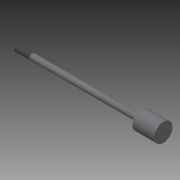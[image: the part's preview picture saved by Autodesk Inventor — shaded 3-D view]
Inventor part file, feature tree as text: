
AUTODESK INVENTOR PART (.ipt)
format: ipt  version: 2014 (Build 180170000, 170)  size: 125,440 bytes
history: native  units: in
note: dims shown in document units (in); Inventor stores cm internally (conversion verified against a paired STEP export)
features: other x49, revolve x3, sketch x3, thread x1
ambient origin geometry x8: Origin, YZ Plane, XZ Plane, XY Plane, X Axis, Y Axis, Z Axis, Center Point
bodies: Solid1 (feature_tree)
feature tree (56):
  revolve  "Revolution1"  [1 undecoded]
  thread  "Thread1"  [1 undecoded]
  revolve  "Revolution2"  [1 undecoded]
  revolve  "Revolution3"  [1 undecoded]
  other  "h1_XY"
  other  "h1_YZ"
  other  "h1_ZX"
  other  "h1_X"
  other  "h1_Y"
  other  "h1_Z"
  other  "h1_Center"
  other  "h2_XY"
  other  "h2_YZ"
  other  "h2_ZX"
  other  "h2_X"
  other  "h2_Y"
  other  "h2_Z"
  other  "h2_Center"
  other  "k1_XY"
  other  "k1_YZ"
  other  "k1_ZX"
  other  "k1_X"
  other  "k1_Y"
  other  "k1_Z"
  other  "k1_Center"
  other  "k2_XY"
  other  "k2_YZ"
  other  "k2_ZX"
  other  "k2_X"
  other  "k2_Y"
  other  "k2_Z"
  other  "k2_Center"
  other  "start_XY"
  other  "start_YZ"
  other  "start_ZX"
  other  "start_X"
  other  "start_Y"
  other  "start_Z"
  other  "start_Center"
  other  "to_prc_XY"
  other  "to_prc_YZ"
  other  "to_prc_ZX"
  other  "to_prc_X"
  other  "to_prc_Y"
  other  "to_prc_Z"
  other  "to_prc_Center"
  other  "to_rod_guide_XY"
  other  "to_rod_guide_YZ"
  other  "to_rod_guide_ZX"
  other  "to_rod_guide_X"
  other  "to_rod_guide_Y"
  other  "to_rod_guide_Z"
  other  "to_rod_guide_Center"
  sketch  "Sketch_3"  dims[d0=360.0deg d1=0.49in d2=4.041in d3=360.0deg]
  sketch  "Sketch_17"
  sketch  "Sketch_12"  dims[d4=360.0deg]
note: 4 required parameter values undecoded (feature->parameter linkage not recoverable at this tier; creation-order binding heuristic only, values carry confidence <= 0.55)